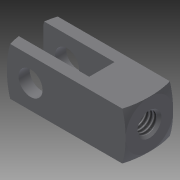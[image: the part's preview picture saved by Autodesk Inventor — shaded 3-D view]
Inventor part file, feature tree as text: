
AUTODESK INVENTOR PART (.ipt)
format: ipt  version: 2014 (Build 180170000, 170)  size: 189,440 bytes
history: native  units: in
note: dims shown in document units (in); Inventor stores cm internally (conversion verified against a paired STEP export)
features: other x126, sketch x7, hole x3, extrude x2, revolve x2
ambient origin geometry x8: Origin, YZ Plane, XZ Plane, XY Plane, X Axis, Y Axis, Z Axis, Center Point
bodies: Solid1 (feature_tree)
feature tree (140):
  extrude  "Extrusion1"  Depth=0.375in TaperAngle=0.0deg
  extrude  "Extrusion2"  TaperAngle=360.0deg  [1 undecoded]
  hole  "Hole1"  [1 undecoded]
  hole  "Hole2"  [1 undecoded]
  hole  "Hole3"  [1 undecoded]
  revolve  "Revolution1"  [1 undecoded]
  revolve  "Revolution2"  [1 undecoded]
  other  "dummy_XY"
  other  "dummy_YZ"
  other  "dummy_ZX"
  other  "dummy_X"
  other  "dummy_Y"
  other  "dummy_Z"
  other  "dummy_Center"
  other  "h1_XY"
  other  "h1_YZ"
  other  "h1_ZX"
  other  "h1_X"
  other  "h1_Y"
  other  "h1_Z"
  other  "h1_Center"
  other  "h2_XY"
  other  "h2_YZ"
  other  "h2_ZX"
  other  "h2_X"
  other  "h2_Y"
  other  "h2_Z"
  other  "h2_Center"
  other  "l1_XY"
  other  "l1_YZ"
  other  "l1_ZX"
  other  "l1_X"
  other  "l1_Y"
  other  "l1_Z"
  other  "l1_Center"
  other  "l11_XY"
  other  "l11_YZ"
  other  "l11_ZX"
  other  "l11_X"
  other  "l11_Y"
  other  "l11_Z"
  other  "l11_Center"
  other  "l12_XY"
  other  "l12_YZ"
  other  "l12_ZX"
  other  "l12_X"
  other  "l12_Y"
  other  "l12_Z"
  other  "l12_Center"
  other  "l2_XY"
  other  "l2_YZ"
  other  "l2_ZX"
  other  "l2_X"
  other  "l2_Y"
  other  "l2_Z"
  other  "l2_Center"
  other  "l21_XY"
  other  "l21_YZ"
  other  "l21_ZX"
  other  "l21_X"
  other  "l21_Y"
  other  "l21_Z"
  other  "l21_Center"
  other  "l22_XY"
  other  "l22_YZ"
  other  "l22_ZX"
  other  "l22_X"
  other  "l22_Y"
  other  "l22_Z"
  other  "l22_Center"
  other  "piston_rod_clevis_XY"
  other  "piston_rod_clevis_YZ"
  other  "piston_rod_clevis_ZX"
  other  "piston_rod_clevis_X"
  other  "piston_rod_clevis_Y"
  other  "piston_rod_clevis_Z"
  other  "piston_rod_clevis_Center"
  other  "rod_clevis_body_XY"
  other  "rod_clevis_body_YZ"
  other  "rod_clevis_body_ZX"
  other  "rod_clevis_body_X"
  other  "rod_clevis_body_Y"
  other  "rod_clevis_body_Z"
  other  "rod_clevis_body_Center"
  other  "th1_XY"
  other  "th1_YZ"
  other  "th1_ZX"
  other  "th1_X"
  other  "th1_Y"
  other  "th1_Z"
  other  "th1_Center"
  other  "th2_XY"
  other  "th2_YZ"
  other  "th2_ZX"
  other  "th2_X"
  other  "th2_Y"
  other  "th2_Z"
  other  "th2_Center"
  other  "to_cylinder_XY"
  other  "to_cylinder_YZ"
  other  "to_cylinder_ZX"
  other  "to_cylinder_X"
  other  "to_cylinder_Y"
  other  "to_cylinder_Z"
  other  "to_cylinder_Center"
  other  "w1_XY"
  other  "w1_YZ"
  other  "w1_ZX"
  other  "w1_X"
  other  "w1_Y"
  other  "w1_Z"
  other  "w1_Center"
  other  "w11_XY"
  other  "w11_YZ"
  other  "w11_ZX"
  other  "w11_X"
  other  "w11_Y"
  other  "w11_Z"
  other  "w11_Center"
  other  "w12_XY"
  other  "w12_YZ"
  other  "w12_ZX"
  other  "w12_X"
  other  "w12_Y"
  other  "w12_Z"
  other  "w12_Center"
  other  "w2_XY"
  other  "w2_YZ"
  other  "w2_ZX"
  other  "w2_X"
  other  "w2_Y"
  other  "w2_Z"
  other  "w2_Center"
  sketch  "Sketch_1"  dims[d0=0.375in d1=0.0in d2=0.375in d3=0.0in]
  sketch  "Sketch_2"  dims[d4=0.156in d5=0.31in d6=0.19in d7=0.25in d8=90.0deg d9=0.31in d10=0.0in]
  sketch  "Sketch3"  dims[d11=0.1562in d12=0.75in d13=0.375in d14=0.25in d15=0.5635in d16=0.065in d17=0.0in]
  sketch  "Sketch4"  dims[d18=0.19in d19=0.75in d20=0.375in d21=0.25in d22=0.5635in d23=0.375in d24=0.0in d25=360.0deg]
  sketch  "Sketch5"  dims[d26=360.0deg]
  sketch  "Sketch_9"
  sketch  "Sketch_10"
note: 6 required parameter values undecoded (feature->parameter linkage not recoverable at this tier; creation-order binding heuristic only, values carry confidence <= 0.55)
